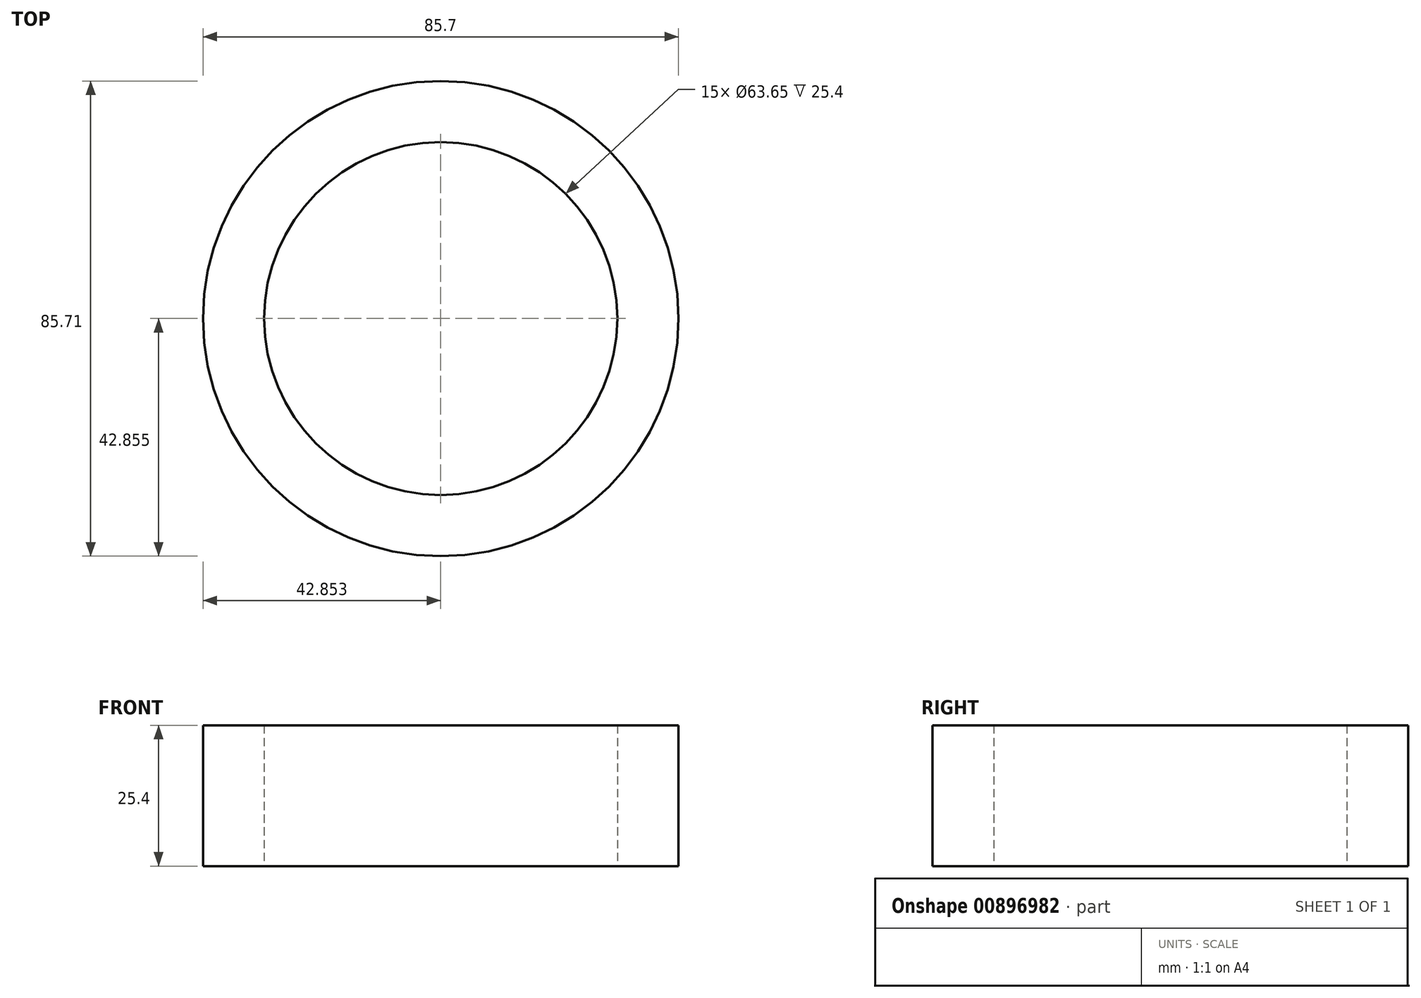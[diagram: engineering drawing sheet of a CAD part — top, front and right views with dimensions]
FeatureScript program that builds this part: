
annotation { "Feature Type Name" : "Feature", "Feature Type Description" : "" }
export const myFeature = defineFeature(function(context is Context, id is Id, definition is map)
    precondition{}
    {
        {
            var Q0;
            Q0=qCreatedBy(makeId("Top.planeOp"),FACE);
            var sketch = newSketch(context, id + "F0", { "sketchPlane" : qUnion([Q0])});
            skCircle(sketch, "E0", {"center": v(-2.59, 13.94) * mm, "radius": 31.82 * mm});
            skCircle(sketch, "E1", {"center": v(-2.59, 13.94) * mm, "radius": 42.85 * mm});
            skSolve(sketch);
        }
        {
            var Q0;
            Q0=makeQuery(id+"F0.imprint","IMPRINT",FACE,{"disambiguationData":[TD([[makeQuery(id+"F0.imprint","IMPRINT",EDGE,{"derivedFrom":sQuery(id+"F0.wireOp",EDGE,"E0")}),-1.0]])]});
            extrude(context, id + "F1", {"entities" : qUnion([Q0]), "depth" : 25.4 * mm, "offsetDistance" : 25.4 * mm});
        }
    });
